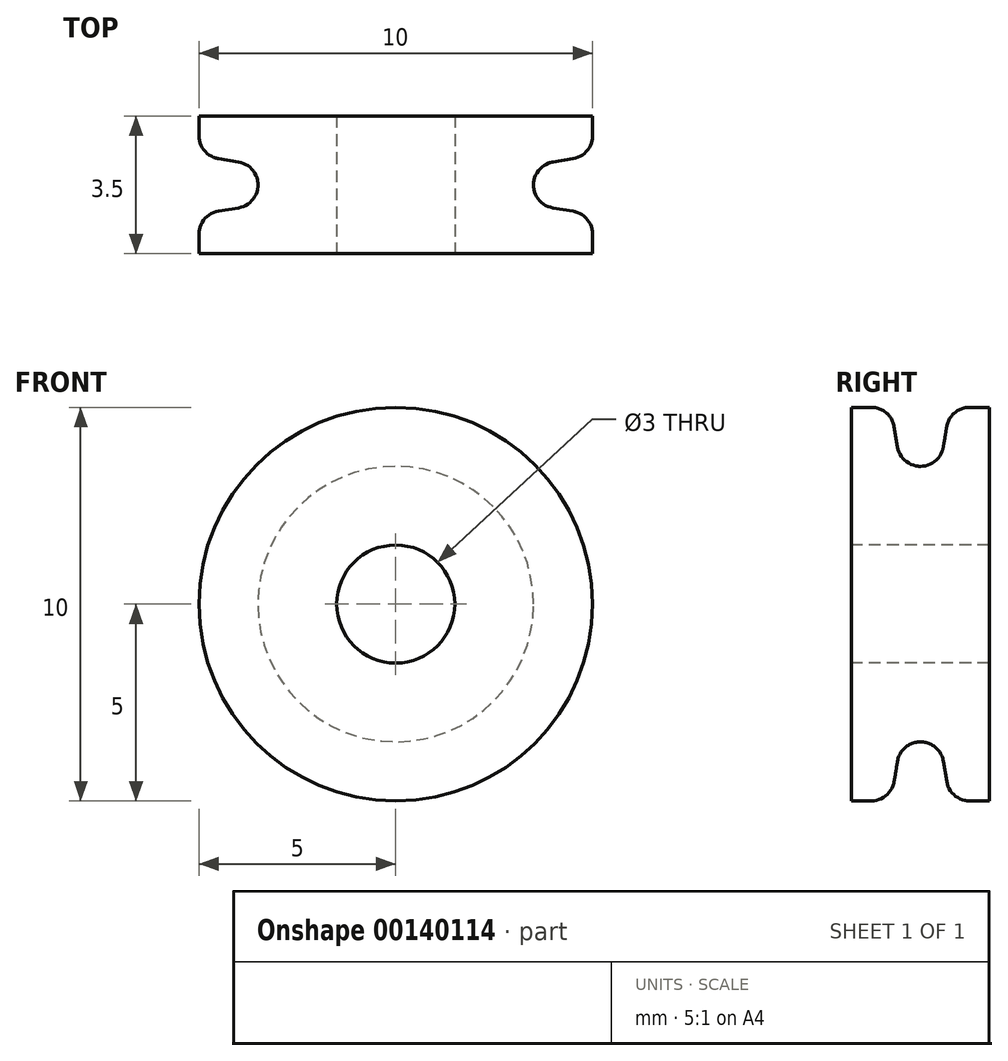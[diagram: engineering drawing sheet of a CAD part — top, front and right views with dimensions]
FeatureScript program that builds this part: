
annotation { "Feature Type Name" : "Feature", "Feature Type Description" : "" }
export const myFeature = defineFeature(function(context is Context, id is Id, definition is map)
    precondition{}
    {
        {
            var Q0;
            Q0=qCreatedBy(makeId("Right.planeOp"),FACE);
            var sketch = newSketch(context, id + "F0", { "sketchPlane" : qUnion([Q0])});
            skLineSegment(sketch, "E0", {"start": v(0, 1.5) * mm, "end": v(0, 5) * mm});
            skLineSegment(sketch, "E1", {"start": v(0, 5) * mm, "end": v(1, 5) * mm});
            skLineSegment(sketch, "E2", {"start": v(1, 5) * mm, "end": v(1.25, 3.5) * mm});
            skLineSegment(sketch, "E3", {"start": v(1.25, 3.5) * mm, "end": v(2.25, 3.5) * mm});
            skLineSegment(sketch, "E4", {"start": v(2.25, 3.5) * mm, "end": v(2.5, 5) * mm});
            skLineSegment(sketch, "E5.trimOffspring", {"start": v(2.5, 5) * mm, "end": v(3.5, 5) * mm});
            skLineSegment(sketch, "E6", {"start": v(0, 1.5) * mm, "end": v(3.5, 1.5) * mm});
            skLineSegment(sketch, "E7", {"start": v(3.5, 5) * mm, "end": v(3.5, 1.5) * mm});
            skLineSegment(sketch, "E8", {"start": v(0, 0) * mm, "end": v(3.5, 0) * mm});
            skSolve(sketch);
        }
        {
            var Q0;
            Q0=makeQuery(id+"F0.imprint","IMPRINT",FACE,{"disambiguationData":[TD([[makeQuery(id+"F0.imprint","IMPRINT",EDGE,{"derivedFrom":sQuery(id+"F0.wireOp",EDGE,"E0")}),-1.0]])]});
            var Q1;
            Q1=sQuery(id+"F0.wireOp",EDGE,"E8");
            revolve(context, id + "F1", {"entities" : qUnion([Q0]), "axis" : qUnion([Q1]), "revolveType" : RevolveType.FULL});
        }
        {
            var Q0;
            Q0=makeQuery(id+"F1.opRevolve","SWEPT_FACE",FACE,{"disambiguationData":[OSD([sQuery(id+"F0.wireOp",EDGE,"E2")])]});
            var Q1;
            Q1=makeQuery(id+"F1.opRevolve","SWEPT_FACE",FACE,{"disambiguationData":[OSD([sQuery(id+"F0.wireOp",EDGE,"E4")])]});
            fillet(context, id + "F2", {"entities" : qUnion([Q0, Q1]), "radius" : .59 * mm, "tangentPropagation" : true, "allowEdgeOverflow" : false});
        }
    });
